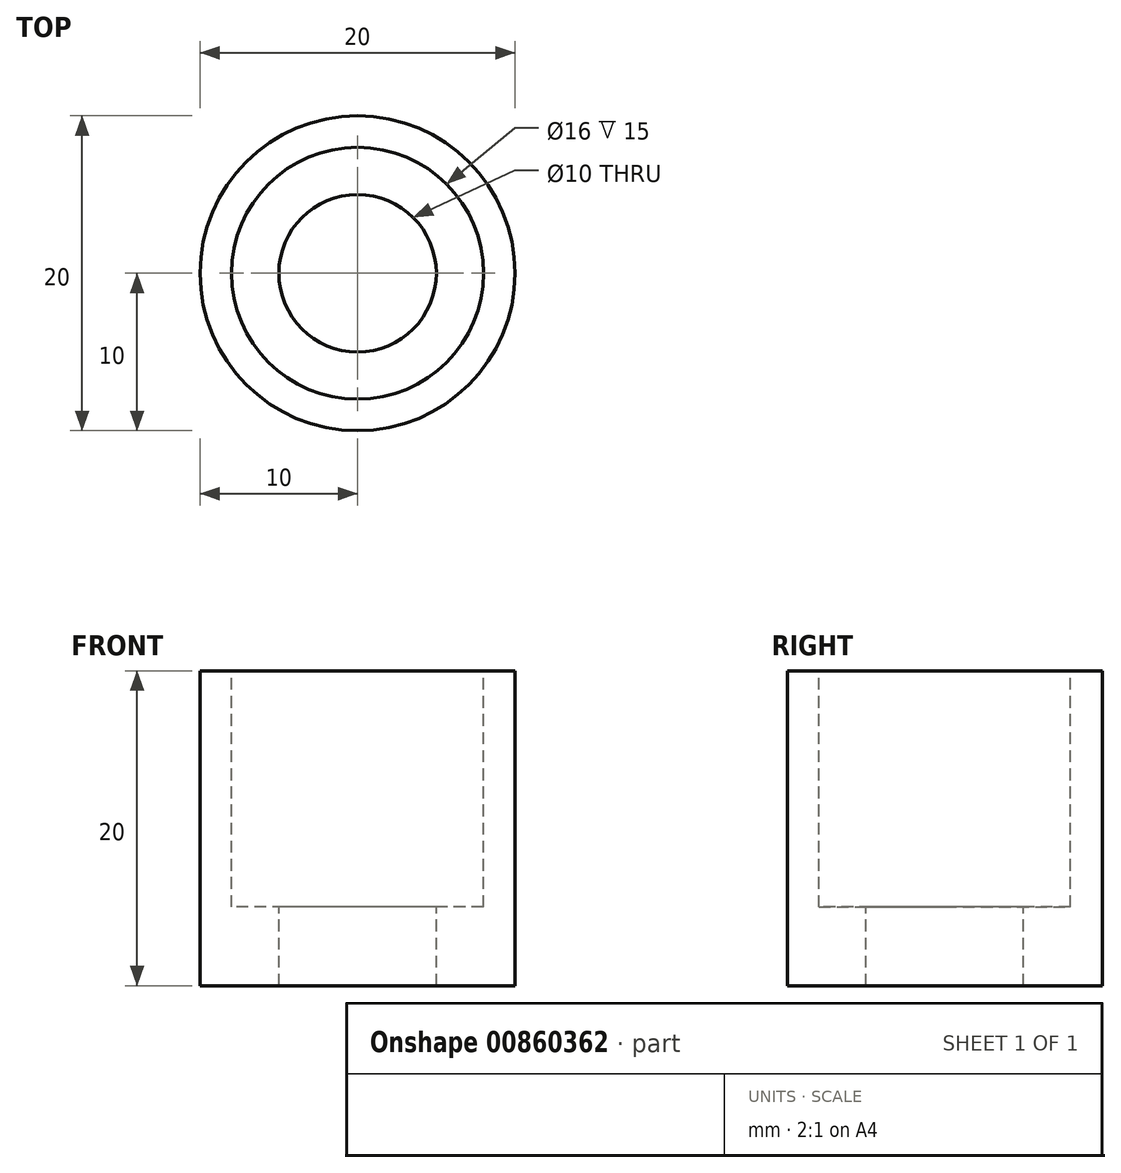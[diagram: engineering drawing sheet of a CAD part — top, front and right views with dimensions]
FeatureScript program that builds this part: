
annotation { "Feature Type Name" : "Feature", "Feature Type Description" : "" }
export const myFeature = defineFeature(function(context is Context, id is Id, definition is map)
    precondition{}
    {
        {
            var Q0;
            Q0=qCreatedBy(makeId("Right.planeOp"),FACE);
            var sketch = newSketch(context, id + "F0", { "sketchPlane" : qUnion([Q0])});
            skLineSegment(sketch, "E0.bottom", {"start": v(8, 0) * mm, "end": v(10, 0) * mm});
            skLineSegment(sketch, "E0.top", {"start": v(5, -20) * mm, "end": v(10, -20) * mm});
            skLineSegment(sketch, "E0.right", {"start": v(10, 0) * mm, "end": v(10, -20) * mm});
            skLineSegment(sketch, "E1.top", {"start": v(8, -15) * mm, "end": v(5, -15) * mm});
            skLineSegment(sketch, "E1.left", {"start": v(8, 0) * mm, "end": v(8, -15) * mm});
            skPoint(sketch, "E2.firstSnap0", {"position": v(5, -20) * mm});
            skLineSegment(sketch, "E2.left", {"start": v(5, -15) * mm, "end": v(5, -20) * mm});
            skPoint(sketch, "E3.orphan", {"position": v(0, -20) * mm});
            skSolve(sketch);
        }
        {
            var Q0;
            Q0=qCreatedBy(makeId("Right.planeOp"),FACE);
            var sketch = newSketch(context, id + "F1", { "sketchPlane" : qUnion([Q0])});
            skLineSegment(sketch, "E4", {"start": v(0, 79.59) * mm, "end": v(0, -89.29) * mm, "construction": true});
            skSolve(sketch);
        }
        {
            var Q0;
            Q0=makeQuery(id+"F0.imprint","IMPRINT",FACE,{"disambiguationData":[TD([[makeQuery(id+"F0.imprint","IMPRINT",EDGE,{"derivedFrom":sQuery(id+"F0.wireOp",EDGE,"E0.bottom")}),-1.0]])]});
            var Q1;
            Q1=sQuery(id+"F1.wireOp",EDGE,"E4");
            revolve(context, id + "F2", {"surfaceOperationType" : NewSurfaceOperationType.NEW, "entities" : qUnion([Q0]), "axis" : qUnion([Q1]), "revolveType" : RevolveType.FULL});
        }
    });
